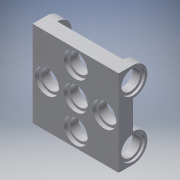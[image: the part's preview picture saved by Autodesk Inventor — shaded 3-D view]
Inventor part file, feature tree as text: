
AUTODESK INVENTOR PART (.ipt)
format: ipt  version: 2017 (Build 210142000, 142)  size: 246,784 bytes
history: native  units: mm
features: extrude x7, sketch x7, plane x2, mirror x2
ambient origin geometry x8: Origin, YZ Plane, XZ Plane, XY Plane, X Axis, Y Axis, Z Axis, Center Point
bodies: Solid1 (feature_tree)
feature tree (18):
  extrude  "Extrusion1"  Depth=18.0mm
  extrude  "Extrusion2"  Depth=6.0mm
  extrude  "Extrusion3"  Depth=40.0mm TaperAngle=360.0deg
  extrude  "Extrusion4"  Depth=3.0mm
  extrude  "Extrusion5"  Depth=40.0mm TaperAngle=360.0deg
  extrude  "Extrusion6"  Depth=0.8mm TaperAngle=360.0deg
  extrude  "Extrusion7"  Depth=3.0mm
  plane  "Work Plane1"
  plane  "Work Plane2"
  mirror  "Mirror1"
  mirror  "Mirror2"
  sketch  "Sketch1"  dims[d0=18.0mm d1=18.0mm]
  sketch  "Sketch2"  dims[d2=4.0mm d3=6.0mm]
  sketch  "Sketch3"  dims[d8=4.0mm d9=40.0mm d11=360.0deg]
  sketch  "Sketch4"  dims[d13=3.0mm d14=0.0mm d15=5.0mm]
  sketch  "Sketch5"  dims[d16=5.0mm d17=40.0mm d19=360.0deg]
  sketch  "Sketch6"  dims[d21=0.8mm d22=0.0mm d23=40.0mm d25=360.0deg]
  sketch  "Sketch7"  dims[d27=0.8mm d28=0.0mm d29=3.0mm d30=2.15mm d31=0.0mm d32=4.0mm d33=3.0mm d34=0.0mm d35=5.0mm d36=0.5mm d37=0.0mm d38=5.0mm d39=1.0mm d40=1.0mm d41=0.0mm d42=0.0mm]
